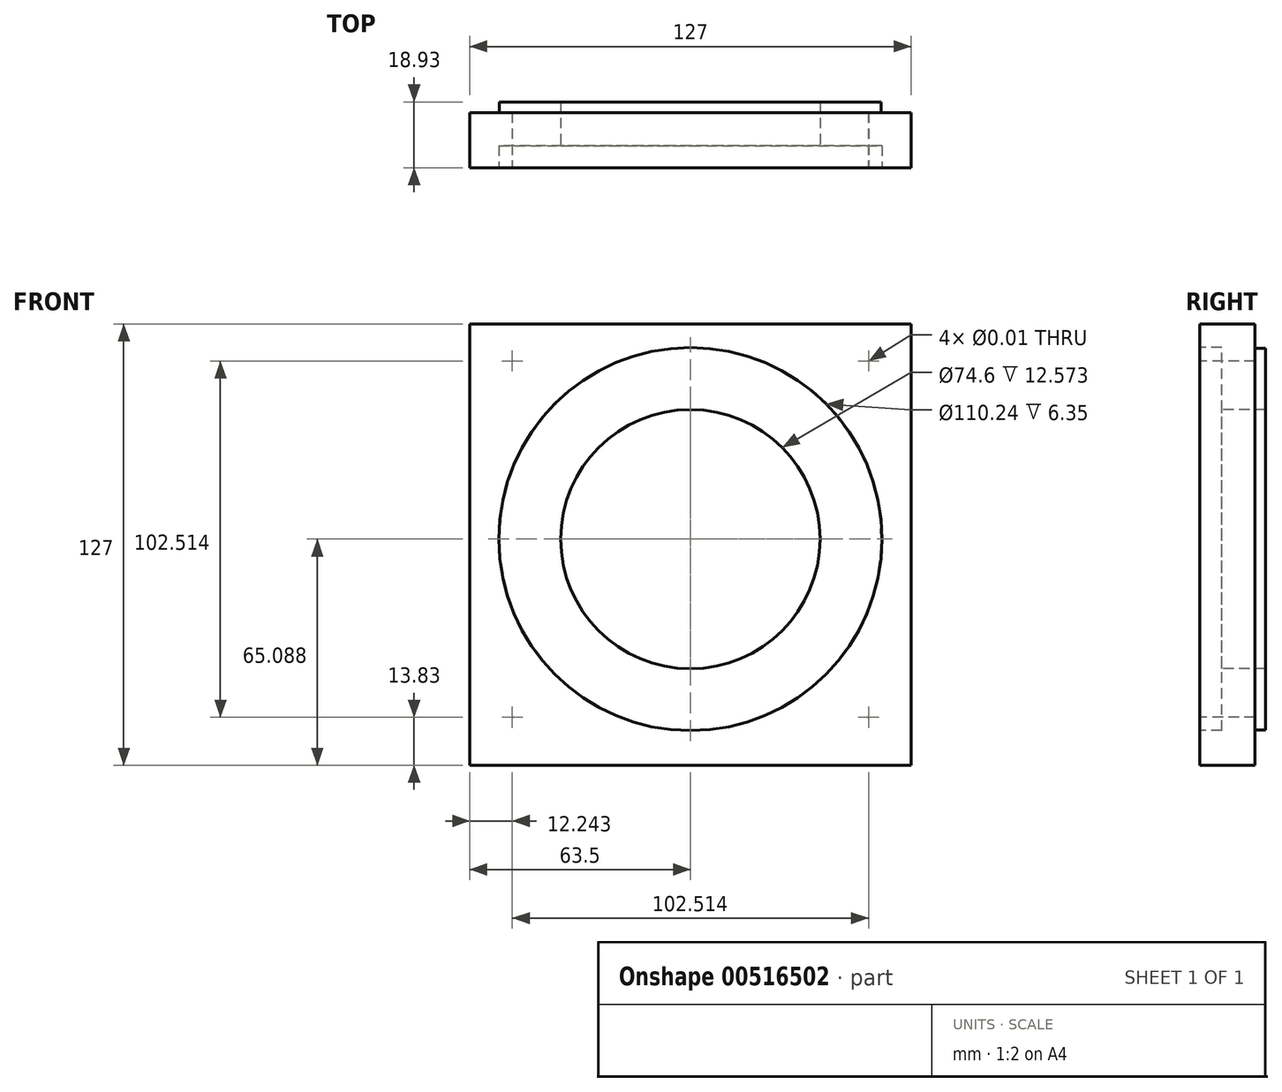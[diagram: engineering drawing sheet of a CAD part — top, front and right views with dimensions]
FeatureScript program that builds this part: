
annotation { "Feature Type Name" : "Feature", "Feature Type Description" : "" }
export const myFeature = defineFeature(function(context is Context, id is Id, definition is map)
    precondition{}
    {
        {
            var Q0;
            Q0=qCreatedBy(makeId("Front.planeOp"),FACE);
            var sketch = newSketch(context, id + "F0", { "sketchPlane" : qUnion([Q0])});
            skLineSegment(sketch, "E0.bottom", {"start": v(0, 0) * mm, "end": v(-127, 0) * mm});
            skLineSegment(sketch, "E0.top", {"start": v(0, 127) * mm, "end": v(-127, 127) * mm});
            skLineSegment(sketch, "E0.left", {"start": v(0, 0) * mm, "end": v(0, 127) * mm});
            skLineSegment(sketch, "E0.right", {"start": v(-127, 0) * mm, "end": v(-127, 127) * mm});
            skSolve(sketch);
        }
        {
            var Q0;
            Q0=makeQuery(id+"F0.imprint","IMPRINT",FACE,{"disambiguationData":[TD([[makeQuery(id+"F0.imprint","IMPRINT",EDGE,{"derivedFrom":sQuery(id+"F0.wireOp",EDGE,"E0.bottom")}),-1.0]])]});
            var sketch = newSketch(context, id + "F1", { "sketchPlane" : qUnion([Q0])});
            skSolve(sketch);
        }
        {
            var Q0;
            Q0=makeQuery(id+"F0.imprint","IMPRINT",FACE,{"disambiguationData":[TD([[makeQuery(id+"F0.imprint","IMPRINT",EDGE,{"derivedFrom":sQuery(id+"F0.wireOp",EDGE,"E0.bottom")}),-1.0]])]});
            extrude(context, id + "F2", {"entities" : qUnion([Q0]), "depth" : 15.88 * mm, "offsetDistance" : 25.4 * mm});
        }
        {
            var Q0;
            Q0=makeQuery(id+"F2.opExtrude","CAP_FACE",FACE,{"disambiguationData":[OSD([sQuery(id+"F0.wireOp",EDGE,"E0.bottom"),sQuery(id+"F0.wireOp",EDGE,"E0.top"),sQuery(id+"F0.wireOp",EDGE,"E0.left"),sQuery(id+"F0.wireOp",EDGE,"E0.right")])],"isStart":false});
            var sketch = newSketch(context, id + "F3", { "sketchPlane" : qUnion([Q0])});
            skPoint(sketch, "E1", {"position": v(-63.5, 65.09) * mm});
            skCircle(sketch, "E2", {"center": v(-63.5, 65.09) * mm, "radius": 37.3 * mm});
            skSolve(sketch);
        }
        {
            var Q0;
            Q0=makeQuery(id+"F3.imprint","IMPRINT",FACE,{"disambiguationData":[TD([[makeQuery(id+"F3.imprint","IMPRINT",EDGE,{"derivedFrom":sQuery(id+"F3.wireOp",EDGE,"E2")}),1.0]])]});
            extrude(context, id + "F4", {"entities" : qUnion([Q0]), "operationType" : NewBodyOperationType.REMOVE, "oppositeDirection" : true, "depth" : 16 * mm, "offsetDistance" : 25.4 * mm});
        }
        {
            var Q0;
            Q0=makeQuery(id+"F2.opExtrude","CAP_FACE",FACE,{"disambiguationData":[OSD([sQuery(id+"F0.wireOp",EDGE,"E0.bottom"),sQuery(id+"F0.wireOp",EDGE,"E0.top"),sQuery(id+"F0.wireOp",EDGE,"E0.left"),sQuery(id+"F0.wireOp",EDGE,"E0.right")])],"isStart":false});
            var sketch = newSketch(context, id + "F5", { "sketchPlane" : qUnion([Q0])});
            skCircle(sketch, "E3", {"center": v(-63.5, 65.09) * mm, "radius": 55.12 * mm});
            skSolve(sketch);
        }
        {
            var Q0;
            Q0=makeQuery(id+"F5.imprint","IMPRINT",FACE,{"disambiguationData":[TD([[makeQuery(id+"F5.imprint","IMPRINT",EDGE,{"derivedFrom":sQuery(id+"F5.wireOp",EDGE,"E3")}),1.0]])]});
            extrude(context, id + "F6", {"entities" : qUnion([Q0]), "operationType" : NewBodyOperationType.REMOVE, "oppositeDirection" : true, "depth" : 6.35 * mm, "offsetDistance" : 25.4 * mm});
        }
        {
            var Q0;
            Q0=makeQuery(id+"F1.imprint","IMPRINT",FACE,{"disambiguationData":[TD([[makeQuery(id+"F1.imprint","IMPRINT",EDGE,{"derivedFrom":makeQuery(id+"F0.imprint","IMPRINT",EDGE,{"derivedFrom":sQuery(id+"F0.wireOp",EDGE,"E0.bottom")})}),-1.0]])]});
            var sketch = newSketch(context, id + "F7", { "sketchPlane" : qUnion([Q0])});
            skCircle(sketch, "E4", {"center": v(-63.5, 65.09) * mm, "radius": 54.93 * mm});
            skCircle(sketch, "E5", {"center": v(-63.5, 65.09) * mm, "radius": 37.3 * mm});
            skSolve(sketch);
        }
        {
            var Q0;
            Q0 = qSketchRegion(id + "F7", true);
            extrude(context, id + "F8", {"entities" : qUnion([Q0]), "operationType" : NewBodyOperationType.ADD, "oppositeDirection" : true, "depth" : 3.05 * mm, "offsetDistance" : 25.4 * mm});
        }
        {
            var Q0;
            Q0=makeQuery(id+"F2.opExtrude","CAP_FACE",FACE,{"disambiguationData":[OSD([sQuery(id+"F0.wireOp",EDGE,"E0.bottom"),sQuery(id+"F0.wireOp",EDGE,"E0.top"),sQuery(id+"F0.wireOp",EDGE,"E0.left"),sQuery(id+"F0.wireOp",EDGE,"E0.right")])],"isStart":false});
            var sketch = newSketch(context, id + "F9", { "sketchPlane" : qUnion([Q0])});
            skPoint(sketch, "E6", {"position": v(-114.76, 116.34) * mm});
            skPoint(sketch, "E7", {"position": v(-12.24, 116.34) * mm});
            skPoint(sketch, "E8", {"position": v(-12.24, 13.83) * mm});
            skPoint(sketch, "E9", {"position": v(-114.76, 13.83) * mm});
            skPoint(sketch, "E10", {"position": v(-63.5, 65.09) * mm});
            skSolve(sketch);
        }
        {
            var Q0;
            Q0=sQuery(id+"F9.wireOp",VERTEX,"E6");
            var Q1;
            Q1=sQuery(id+"F9.wireOp",VERTEX,"E7");
            var Q2;
            Q2=sQuery(id+"F9.wireOp",VERTEX,"E8");
            var Q3;
            Q3=sQuery(id+"F9.wireOp",VERTEX,"E9");
            var Q4;
            Q4=makeQuery(id+"F2.opExtrude","SWEPT_BODY",BODY,{"disambiguationData":[OSD([sQuery(id+"F0.wireOp",EDGE,"E0.bottom"),sQuery(id+"F0.wireOp",EDGE,"E0.top"),sQuery(id+"F0.wireOp",EDGE,"E0.left"),sQuery(id+"F0.wireOp",EDGE,"E0.right")])]});
            hole(context, id + "F10", {"style" : HoleStyle.SIMPLE, "endStyle" : HoleEndStyle.THROUGH, "standardTappedOrClearance" : lookupTablePath({ "standard" : "ANSI", "size" : "11/32 (0.34)", "type" : "Drilled" }), "standardBlindInLast" : lookupTablePath({ "standard" : "ANSI", "size" : "11/32", "type" : "Drilled" }), "holeDiameter" : 11 / 812.8 * mm, "isTappedThrough" : true, "tappedDepth" : 8.9 * mm, "tapClearance" : 1, "locations" : qUnion([Q0, Q1, Q2, Q3]), "scope" : qUnion([Q4])});
        }
    });
